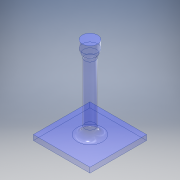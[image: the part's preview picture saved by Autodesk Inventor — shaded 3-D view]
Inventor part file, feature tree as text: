
AUTODESK INVENTOR PART (.ipt)
format: ipt  version: 2017 (Build 210142000, 142)  size: 138,752 bytes
history: native  units: mm
features: sketch x4, extrude x3, fillet x2
ambient origin geometry x8: Origin, YZ Plane, XZ Plane, XY Plane, X Axis, Y Axis, Z Axis, Center Point
bodies: Solid1 (feature_tree)
feature tree (9):
  extrude  "Extrusion1"  Depth=70.0mm TaperAngle=0.0deg
  extrude  "Extrusion2"  Depth=10.0mm TaperAngle=0.0deg
  fillet  "Fillet1"  Radius=7.25mm
  extrude  "Extrusion3"  Depth=55.0mm
  fillet  "Fillet2"  Radius=5.0mm
  sketch  "3D Sketch1"
  sketch  "Sketch1"  dims[d0=10.0mm d1=70.0mm d2=0.0mm]
  sketch  "Sketch2"  dims[d3=15.0mm d4=10.0mm d5=0.0mm d6=7.25mm]
  sketch  "Sketch3"  dims[d7=55.0mm d8=55.0mm d9=5.0mm d10=0.0mm d11=7.25mm]
